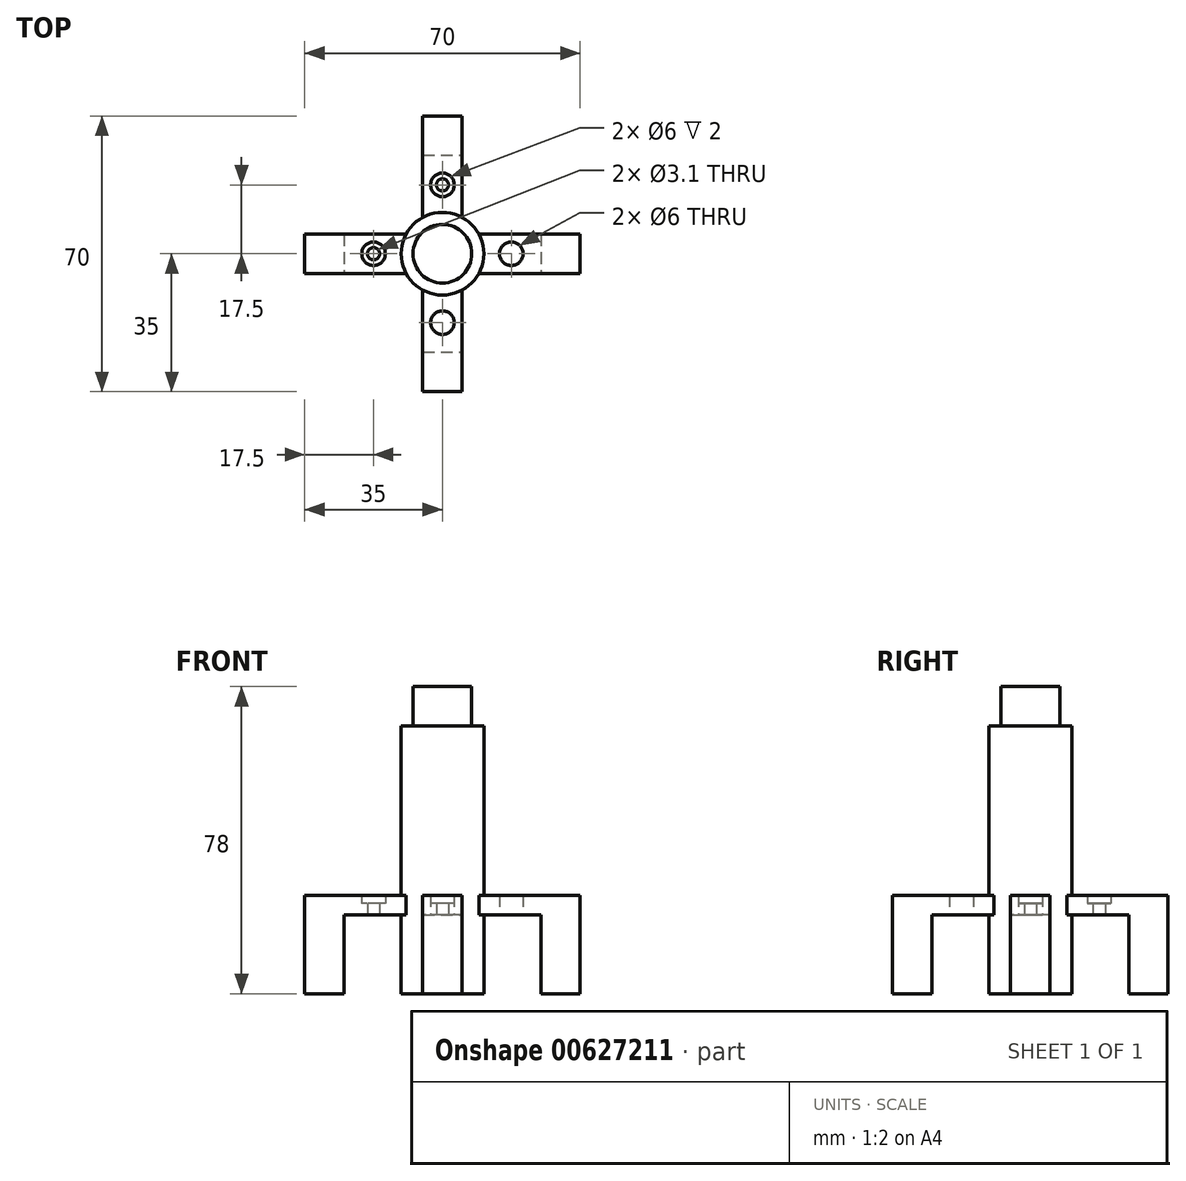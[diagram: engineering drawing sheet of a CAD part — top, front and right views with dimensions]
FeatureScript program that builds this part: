
annotation { "Feature Type Name" : "Feature", "Feature Type Description" : "" }
export const myFeature = defineFeature(function(context is Context, id is Id, definition is map)
    precondition{}
    {
        {
            var Q0;
            Q0=qCreatedBy(makeId("Top.planeOp"),FACE);
            var sketch = newSketch(context, id + "F0", { "sketchPlane" : qUnion([Q0])});
            skCircle(sketch, "E0", {"center": v(0, 0) * mm, "radius": 7.45 * mm});
            skCircle(sketch, "E1", {"center": v(0, 0) * mm, "radius": 10.5 * mm});
            skLineSegment(sketch, "E2.bottom", {"start": v(5, -5) * mm, "end": v(-5, -5) * mm});
            skLineSegment(sketch, "E2.top", {"start": v(5, 5) * mm, "end": v(-5, 5) * mm});
            skLineSegment(sketch, "E2.left", {"start": v(5, -5) * mm, "end": v(5, 5) * mm});
            skLineSegment(sketch, "E2.right", {"start": v(-5, -5) * mm, "end": v(-5, 5) * mm});
            skLineSegment(sketch, "E3", {"start": v(5, 5) * mm, "end": v(35, 5) * mm});
            skLineSegment(sketch, "E4", {"start": v(35, 5) * mm, "end": v(35, -5) * mm});
            skLineSegment(sketch, "E5", {"start": v(35, -5) * mm, "end": v(5, -5) * mm});
            skLineSegment(sketch, "E6", {"start": v(5, -5) * mm, "end": v(5, -35) * mm});
            skLineSegment(sketch, "E7", {"start": v(5, -35) * mm, "end": v(-5, -35) * mm});
            skLineSegment(sketch, "E8", {"start": v(-5, -35) * mm, "end": v(-5, -5) * mm});
            skLineSegment(sketch, "E9.MirrorCS", {"start": v(-5, 5) * mm, "end": v(-35, 5) * mm});
            skLineSegment(sketch, "E10.MirrorCS", {"start": v(-35, 5) * mm, "end": v(-35, -5) * mm});
            skLineSegment(sketch, "E11.MirrorCS", {"start": v(-35, -5) * mm, "end": v(-5, -5) * mm});
            skLineSegment(sketch, "E12.MirrorCS", {"start": v(-5, 35) * mm, "end": v(-5, 5) * mm});
            skLineSegment(sketch, "E13.MirrorCS", {"start": v(5, 35) * mm, "end": v(-5, 35) * mm});
            skLineSegment(sketch, "E14.MirrorCS", {"start": v(5, 5) * mm, "end": v(5, 35) * mm});
            skLineSegment(sketch, "E15", {"start": v(-25, 5) * mm, "end": v(-25, -5) * mm});
            skPoint(sketch, "E15.endSnap0", {"position": v(-20, -5) * mm});
            skLineSegment(sketch, "E16", {"start": v(-5, 25) * mm, "end": v(5, 25) * mm});
            skLineSegment(sketch, "E17.MirrorCS", {"start": v(25, 5) * mm, "end": v(25, -5) * mm});
            skLineSegment(sketch, "E18.MirrorCS", {"start": v(-5, -25) * mm, "end": v(5, -25) * mm});
            skCircle(sketch, "E19", {"center": v(-17.5, 0) * mm, "radius": 1.55 * mm});
            skPoint(sketch, "E19.centerSnap0", {"position": v(-25, 0) * mm});
            skCircle(sketch, "E20", {"center": v(-17.5, 0) * mm, "radius": 3 * mm});
            skCircle(sketch, "E21", {"center": v(0, 17.5) * mm, "radius": 1.55 * mm});
            skCircle(sketch, "E22", {"center": v(0, 17.5) * mm, "radius": 3 * mm});
            skCircle(sketch, "E23.MirrorC", {"center": v(17.5, 0) * mm, "radius": 3 * mm});
            skCircle(sketch, "E24.MirrorC", {"center": v(17.5, 0) * mm, "radius": 1.55 * mm});
            skCircle(sketch, "E25.MirrorC", {"center": v(0, -17.5) * mm, "radius": 3 * mm});
            skCircle(sketch, "E26.MirrorC", {"center": v(0, -17.5) * mm, "radius": 1.55 * mm});
            skSolve(sketch);
        }
        {
            var Q0;
            {var subQ0=sQuery(id+"F0.wireOp",EDGE,"E15");Q0=makeQuery(id+"F0.imprint","IMPRINT",FACE,{"disambiguationData":[TD([[makeQuery(id+"F0.imprint","IMPRINT",EDGE,{"derivedFrom":subQ0}),1.0]])]});}
            var Q1;
            {var subQ0=sQuery(id+"F0.wireOp",EDGE,"E16");Q1=makeQuery(id+"F0.imprint","IMPRINT",FACE,{"disambiguationData":[TD([[makeQuery(id+"F0.imprint","IMPRINT",EDGE,{"derivedFrom":subQ0}),-1.0]])]});}
            var Q2;
            {var subQ0=sQuery(id+"F0.wireOp",EDGE,"E17.MirrorCS");Q2=makeQuery(id+"F0.imprint","IMPRINT",FACE,{"disambiguationData":[TD([[makeQuery(id+"F0.imprint","IMPRINT",EDGE,{"derivedFrom":subQ0}),-1.0]])]});}
            var Q3;
            {var subQ0=sQuery(id+"F0.wireOp",EDGE,"E18.MirrorCS");Q3=makeQuery(id+"F0.imprint","IMPRINT",FACE,{"disambiguationData":[TD([[makeQuery(id+"F0.imprint","IMPRINT",EDGE,{"derivedFrom":subQ0}),1.0]])]});}
            extrude(context, id + "F1", {"entities" : qUnion([Q0, Q1, Q2, Q3]), "depth" : 5 * mm, "offsetDistance" : 25 * mm});
        }
        {
            var Q0;
            Q0=makeQuery(id+"F0.imprint","IMPRINT",FACE,{"disambiguationData":[TD([[makeQuery(id+"F0.imprint","IMPRINT",EDGE,{"derivedFrom":sQuery(id+"F0.wireOp",EDGE,"E21")}),-1.0]])]});
            var Q1;
            Q1=makeQuery(id+"F0.imprint","IMPRINT",FACE,{"disambiguationData":[TD([[makeQuery(id+"F0.imprint","IMPRINT",EDGE,{"derivedFrom":sQuery(id+"F0.wireOp",EDGE,"E23.MirrorC")}),-1.0]])]});
            var Q2;
            Q2=makeQuery(id+"F0.imprint","IMPRINT",FACE,{"disambiguationData":[TD([[makeQuery(id+"F0.imprint","IMPRINT",EDGE,{"derivedFrom":sQuery(id+"F0.wireOp",EDGE,"E25.MirrorC")}),-1.0]])]});
            var Q3;
            Q3=makeQuery(id+"F0.imprint","IMPRINT",FACE,{"disambiguationData":[TD([[makeQuery(id+"F0.imprint","IMPRINT",EDGE,{"derivedFrom":sQuery(id+"F0.wireOp",EDGE,"E19")}),-1.0]])]});
            extrude(context, id + "F2", {"entities" : qUnion([Q0, Q1, Q2, Q3]), "operationType" : NewBodyOperationType.ADD, "depth" : 3 * mm, "offsetDistance" : 25 * mm});
        }
        {
            var Q0;
            {var subQ0=sQuery(id+"F0.wireOp",EDGE,"E13.MirrorCS");Q0=makeQuery(id+"F0.imprint","IMPRINT",FACE,{"disambiguationData":[TD([[makeQuery(id+"F0.imprint","IMPRINT",EDGE,{"derivedFrom":subQ0}),1.0]])]});}
            var Q1;
            {var subQ0=sQuery(id+"F0.wireOp",EDGE,"E4");Q1=makeQuery(id+"F0.imprint","IMPRINT",FACE,{"disambiguationData":[TD([[makeQuery(id+"F0.imprint","IMPRINT",EDGE,{"derivedFrom":subQ0}),-1.0]])]});}
            var Q2;
            {var subQ0=sQuery(id+"F0.wireOp",EDGE,"E7");Q2=makeQuery(id+"F0.imprint","IMPRINT",FACE,{"disambiguationData":[TD([[makeQuery(id+"F0.imprint","IMPRINT",EDGE,{"derivedFrom":subQ0}),-1.0]])]});}
            var Q3;
            {var subQ0=sQuery(id+"F0.wireOp",EDGE,"E10.MirrorCS");Q3=makeQuery(id+"F0.imprint","IMPRINT",FACE,{"disambiguationData":[TD([[makeQuery(id+"F0.imprint","IMPRINT",EDGE,{"derivedFrom":subQ0}),1.0]])]});}
            extrude(context, id + "F3", {"entities" : qUnion([Q0, Q1, Q2, Q3]), "operationType" : NewBodyOperationType.ADD, "depth" : 5 * mm, "offsetDistance" : 25 * mm, "hasSecondDirection" : true, "secondDirectionOppositeDirection" : true, "secondDirectionDepth" : 20 * mm});
        }
        {
            var Q0;
            {var subQ0=sQuery(id+"F0.wireOp",EDGE,"E11.MirrorCS");var subQ1=sQuery(id+"F0.wireOp",EDGE,"E0");var subQ2=makeQuery(id+"F0.imprint","INTERSECT",VERTEX,{"derivedFrom":[subQ1,subQ0]});Q0=makeQuery(id+"F0.imprint","IMPRINT",FACE,{"disambiguationData":[TD([[makeQuery(id+"F0.imprint","IMPRINT",EDGE,{"disambiguationData":[TD([[subQ2,-1.0]])],"derivedFrom":subQ1}),-1.0]])]});}
            var Q1;
            {var subQ0=sQuery(id+"F0.wireOp",EDGE,"E9.MirrorCS");var subQ1=sQuery(id+"F0.wireOp",EDGE,"E0");var subQ2=makeQuery(id+"F0.imprint","INTERSECT",VERTEX,{"derivedFrom":[subQ1,subQ0]});Q1=makeQuery(id+"F0.imprint","IMPRINT",FACE,{"disambiguationData":[TD([[makeQuery(id+"F0.imprint","IMPRINT",EDGE,{"disambiguationData":[TD([[subQ2,-1.0]])],"derivedFrom":subQ1}),-1.0]])]});}
            var Q2;
            {var subQ5=sQuery(id+"F0.wireOp",EDGE,"E2.right");Q2=makeQuery(id+"F0.imprint","IMPRINT",FACE,{"disambiguationData":[TD([[makeQuery(id+"F0.imprint","IMPRINT",EDGE,{"derivedFrom":subQ5}),1.0]])]});}
            var Q3;
            {var subQ0=sQuery(id+"F0.wireOp",EDGE,"E11.MirrorCS");var subQ1=sQuery(id+"F0.wireOp",EDGE,"E0");var subQ2=makeQuery(id+"F0.imprint","INTERSECT",VERTEX,{"derivedFrom":[subQ1,subQ0]});Q3=makeQuery(id+"F0.imprint","IMPRINT",FACE,{"disambiguationData":[TD([[makeQuery(id+"F0.imprint","IMPRINT",EDGE,{"disambiguationData":[TD([[subQ2,-1.0]])],"derivedFrom":subQ1}),1.0]])]});}
            var Q4;
            {var subQ5=sQuery(id+"F0.wireOp",EDGE,"E2.bottom");Q4=makeQuery(id+"F0.imprint","IMPRINT",FACE,{"disambiguationData":[TD([[makeQuery(id+"F0.imprint","IMPRINT",EDGE,{"derivedFrom":subQ5}),1.0]])]});}
            var Q5;
            {var subQ0=sQuery(id+"F0.wireOp",EDGE,"E8");var subQ1=sQuery(id+"F0.wireOp",EDGE,"E0");var subQ2=makeQuery(id+"F0.imprint","INTERSECT",VERTEX,{"derivedFrom":[subQ1,subQ0]});Q5=makeQuery(id+"F0.imprint","IMPRINT",FACE,{"disambiguationData":[TD([[makeQuery(id+"F0.imprint","IMPRINT",EDGE,{"disambiguationData":[TD([[subQ2,-1.0]])],"derivedFrom":subQ1}),-1.0]])]});}
            var Q6;
            Q6=makeQuery(id+"F0.imprint","IMPRINT",FACE,{"disambiguationData":[TD([[makeQuery(id+"F0.imprint","IMPRINT",EDGE,{"derivedFrom":sQuery(id+"F0.wireOp",EDGE,"E2.bottom")}),-1.0]])]});
            var Q7;
            {var subQ5=sQuery(id+"F0.wireOp",EDGE,"E2.left");Q7=makeQuery(id+"F0.imprint","IMPRINT",FACE,{"disambiguationData":[TD([[makeQuery(id+"F0.imprint","IMPRINT",EDGE,{"derivedFrom":subQ5}),-1.0]])]});}
            var Q8;
            {var subQ0=sQuery(id+"F0.wireOp",EDGE,"E6");var subQ1=sQuery(id+"F0.wireOp",EDGE,"E0");var subQ2=makeQuery(id+"F0.imprint","INTERSECT",VERTEX,{"derivedFrom":[subQ1,subQ0]});Q8=makeQuery(id+"F0.imprint","IMPRINT",FACE,{"disambiguationData":[TD([[makeQuery(id+"F0.imprint","IMPRINT",EDGE,{"disambiguationData":[TD([[subQ2,-1.0]])],"derivedFrom":subQ1}),-1.0]])]});}
            var Q9;
            {var subQ0=sQuery(id+"F0.wireOp",EDGE,"E6");var subQ1=sQuery(id+"F0.wireOp",EDGE,"E0");var subQ2=makeQuery(id+"F0.imprint","INTERSECT",VERTEX,{"derivedFrom":[subQ1,subQ0]});Q9=makeQuery(id+"F0.imprint","IMPRINT",FACE,{"disambiguationData":[TD([[makeQuery(id+"F0.imprint","IMPRINT",EDGE,{"disambiguationData":[TD([[subQ2,-1.0]])],"derivedFrom":subQ1}),1.0]])]});}
            var Q10;
            {var subQ0=sQuery(id+"F0.wireOp",EDGE,"E3");var subQ1=sQuery(id+"F0.wireOp",EDGE,"E0");var subQ2=makeQuery(id+"F0.imprint","INTERSECT",VERTEX,{"derivedFrom":[subQ1,subQ0]});Q10=makeQuery(id+"F0.imprint","IMPRINT",FACE,{"disambiguationData":[TD([[makeQuery(id+"F0.imprint","IMPRINT",EDGE,{"disambiguationData":[TD([[subQ2,1.0]])],"derivedFrom":subQ1}),-1.0]])]});}
            var Q11;
            {var subQ0=sQuery(id+"F0.wireOp",EDGE,"E14.MirrorCS");var subQ1=sQuery(id+"F0.wireOp",EDGE,"E0");var subQ2=makeQuery(id+"F0.imprint","INTERSECT",VERTEX,{"derivedFrom":[subQ1,subQ0]});Q11=makeQuery(id+"F0.imprint","IMPRINT",FACE,{"disambiguationData":[TD([[makeQuery(id+"F0.imprint","IMPRINT",EDGE,{"disambiguationData":[TD([[subQ2,1.0]])],"derivedFrom":subQ1}),1.0]])]});}
            var Q12;
            {var subQ0=sQuery(id+"F0.wireOp",EDGE,"E14.MirrorCS");var subQ1=sQuery(id+"F0.wireOp",EDGE,"E0");var subQ2=makeQuery(id+"F0.imprint","INTERSECT",VERTEX,{"derivedFrom":[subQ1,subQ0]});Q12=makeQuery(id+"F0.imprint","IMPRINT",FACE,{"disambiguationData":[TD([[makeQuery(id+"F0.imprint","IMPRINT",EDGE,{"disambiguationData":[TD([[subQ2,1.0]])],"derivedFrom":subQ1}),-1.0]])]});}
            var Q13;
            {var subQ5=sQuery(id+"F0.wireOp",EDGE,"E2.top");Q13=makeQuery(id+"F0.imprint","IMPRINT",FACE,{"disambiguationData":[TD([[makeQuery(id+"F0.imprint","IMPRINT",EDGE,{"derivedFrom":subQ5}),-1.0]])]});}
            var Q14;
            {var subQ0=sQuery(id+"F0.wireOp",EDGE,"E14.MirrorCS");var subQ1=sQuery(id+"F0.wireOp",EDGE,"E0");var subQ2=makeQuery(id+"F0.imprint","INTERSECT",VERTEX,{"derivedFrom":[subQ1,subQ0]});Q14=makeQuery(id+"F0.imprint","IMPRINT",FACE,{"disambiguationData":[TD([[makeQuery(id+"F0.imprint","IMPRINT",EDGE,{"disambiguationData":[TD([[subQ2,-1.0]])],"derivedFrom":subQ1}),-1.0]])]});}
            var Q15;
            {var subQ0=sQuery(id+"F0.wireOp",EDGE,"E12.MirrorCS");var subQ1=sQuery(id+"F0.wireOp",EDGE,"E0");var subQ2=makeQuery(id+"F0.imprint","INTERSECT",VERTEX,{"derivedFrom":[subQ1,subQ0]});Q15=makeQuery(id+"F0.imprint","IMPRINT",FACE,{"disambiguationData":[TD([[makeQuery(id+"F0.imprint","IMPRINT",EDGE,{"disambiguationData":[TD([[subQ2,-1.0]])],"derivedFrom":subQ1}),-1.0]])]});}
            var Q16;
            {var subQ0=sQuery(id+"F0.wireOp",EDGE,"E12.MirrorCS");var subQ1=sQuery(id+"F0.wireOp",EDGE,"E0");var subQ2=makeQuery(id+"F0.imprint","INTERSECT",VERTEX,{"derivedFrom":[subQ1,subQ0]});Q16=makeQuery(id+"F0.imprint","IMPRINT",FACE,{"disambiguationData":[TD([[makeQuery(id+"F0.imprint","IMPRINT",EDGE,{"disambiguationData":[TD([[subQ2,-1.0]])],"derivedFrom":subQ1}),1.0]])]});}
            extrude(context, id + "F4", {"entities" : qUnion([Q0, Q1, Q2, Q3, Q4, Q5, Q6, Q7, Q8, Q9, Q10, Q11, Q12, Q13, Q14, Q15, Q16]), "operationType" : NewBodyOperationType.ADD, "depth" : 48 * mm, "offsetDistance" : 25 * mm, "hasSecondDirection" : true, "secondDirectionOppositeDirection" : true, "secondDirectionDepth" : 20 * mm});
        }
        {
            var Q0;
            Q0=makeQuery(id+"F0.imprint","IMPRINT",FACE,{"disambiguationData":[TD([[makeQuery(id+"F0.imprint","IMPRINT",EDGE,{"derivedFrom":sQuery(id+"F0.wireOp",EDGE,"E2.bottom")}),-1.0]])]});
            var Q1;
            {var subQ5=sQuery(id+"F0.wireOp",EDGE,"E2.right");Q1=makeQuery(id+"F0.imprint","IMPRINT",FACE,{"disambiguationData":[TD([[makeQuery(id+"F0.imprint","IMPRINT",EDGE,{"derivedFrom":subQ5}),1.0]])]});}
            var Q2;
            {var subQ5=sQuery(id+"F0.wireOp",EDGE,"E2.top");Q2=makeQuery(id+"F0.imprint","IMPRINT",FACE,{"disambiguationData":[TD([[makeQuery(id+"F0.imprint","IMPRINT",EDGE,{"derivedFrom":subQ5}),-1.0]])]});}
            var Q3;
            {var subQ5=sQuery(id+"F0.wireOp",EDGE,"E2.left");Q3=makeQuery(id+"F0.imprint","IMPRINT",FACE,{"disambiguationData":[TD([[makeQuery(id+"F0.imprint","IMPRINT",EDGE,{"derivedFrom":subQ5}),-1.0]])]});}
            var Q4;
            {var subQ5=sQuery(id+"F0.wireOp",EDGE,"E2.bottom");Q4=makeQuery(id+"F0.imprint","IMPRINT",FACE,{"disambiguationData":[TD([[makeQuery(id+"F0.imprint","IMPRINT",EDGE,{"derivedFrom":subQ5}),1.0]])]});}
            var Q5;
            {var subQ0=sQuery(id+"F0.wireOp",EDGE,"E11.MirrorCS");var subQ1=sQuery(id+"F0.wireOp",EDGE,"E0");var subQ2=makeQuery(id+"F0.imprint","INTERSECT",VERTEX,{"derivedFrom":[subQ1,subQ0]});Q5=makeQuery(id+"F0.imprint","IMPRINT",FACE,{"disambiguationData":[TD([[makeQuery(id+"F0.imprint","IMPRINT",EDGE,{"disambiguationData":[TD([[subQ2,-1.0]])],"derivedFrom":subQ1}),1.0]])]});}
            var Q6;
            {var subQ0=sQuery(id+"F0.wireOp",EDGE,"E6");var subQ1=sQuery(id+"F0.wireOp",EDGE,"E0");var subQ2=makeQuery(id+"F0.imprint","INTERSECT",VERTEX,{"derivedFrom":[subQ1,subQ0]});Q6=makeQuery(id+"F0.imprint","IMPRINT",FACE,{"disambiguationData":[TD([[makeQuery(id+"F0.imprint","IMPRINT",EDGE,{"disambiguationData":[TD([[subQ2,-1.0]])],"derivedFrom":subQ1}),1.0]])]});}
            var Q7;
            {var subQ0=sQuery(id+"F0.wireOp",EDGE,"E14.MirrorCS");var subQ1=sQuery(id+"F0.wireOp",EDGE,"E0");var subQ2=makeQuery(id+"F0.imprint","INTERSECT",VERTEX,{"derivedFrom":[subQ1,subQ0]});Q7=makeQuery(id+"F0.imprint","IMPRINT",FACE,{"disambiguationData":[TD([[makeQuery(id+"F0.imprint","IMPRINT",EDGE,{"disambiguationData":[TD([[subQ2,1.0]])],"derivedFrom":subQ1}),1.0]])]});}
            var Q8;
            {var subQ0=sQuery(id+"F0.wireOp",EDGE,"E12.MirrorCS");var subQ1=sQuery(id+"F0.wireOp",EDGE,"E0");var subQ2=makeQuery(id+"F0.imprint","INTERSECT",VERTEX,{"derivedFrom":[subQ1,subQ0]});Q8=makeQuery(id+"F0.imprint","IMPRINT",FACE,{"disambiguationData":[TD([[makeQuery(id+"F0.imprint","IMPRINT",EDGE,{"disambiguationData":[TD([[subQ2,-1.0]])],"derivedFrom":subQ1}),1.0]])]});}
            extrude(context, id + "F5", {"entities" : qUnion([Q0, Q1, Q2, Q3, Q4, Q5, Q6, Q7, Q8]), "operationType" : NewBodyOperationType.ADD, "depth" : 58 * mm, "offsetDistance" : 25 * mm});
        }
    });
